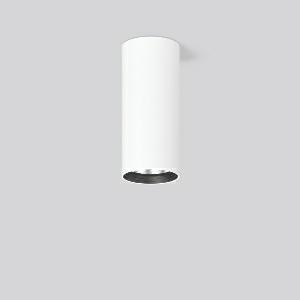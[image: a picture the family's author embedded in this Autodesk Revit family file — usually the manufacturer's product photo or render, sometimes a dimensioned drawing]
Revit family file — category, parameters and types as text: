
# Revit family: heledon_mini_a_931210_002_ff66
name_source: partatom
category: Lighting Fixtures
units: mm (PartAtom-declared; Revit-internal decimal feet)

## family parameters
Cut with Voids When Loaded = No
Host = Face
Light Source = No
Part Type = Normal
Room Calculation Point = No
Round Connector Dimension = Use Diameter
Shared = No

## types (1)
- HELEDON mini A (1 x LED Modul 930, 3650 lm, 3000)
    Apparent Load = 29 VA
    Approval mark = CE
    CIE Flux Codes = 95 99 100 100 100
    Color Rendering = 90
    Color Temperature = 3000
    Default Elevation = 1800 mm
    Description = Series: HELEDON mini
Cylindrical surface-mounted downlight. Housing: die-cast aluminium, powder-coated. Internal ceiling frame polycarbonate with bayonet mounting. Black plastic ring and recessed LED to prevent glare from the side. Optical assembly with reflector made of MIRO-Silver with 98% total light reflection for outstanding efficiency - can be changed without tools. Best colour rendering index Ra>90. Suitable for Ceiling mounting. Easy installation with a separate ceiling frame with bayonet mounting and plug connection. Driver integrated. Connected via plug-in connector. High quality converter without flickering and stroboscopic effect. The following accessories can be mounted without use of tools: interchangeable lenses, decorative glasses, honeycomb louvre, clear and frosted diffusers, white interchangeable plastic ring. 
Colour: traffic white, matt (RAL 9016)
Diameter: 87 mm
Height: 197 mm
Lamp: LED
Socket: without socket
Colour temperature: 3000K
Colour rendering index (CRI): 92
System power: 29 W
Rated luminous flux: 3650 lm
Luminous efficiency: 126 lm/W
Control gear: Regulated power supply
Protection class: I
Type of protection: IP 20
    Height = 197 mm
    Lamp = 1 x LED Modul 930
    Lamp Light Flux = 3650 lm
    Lamp count = 1
    Length = 87 mm
    Lifetime = 50000 h
    Luminous efficacy = 126 lm/W
    Manufacturer = RZB
    ModVariant = No
    Model = 931210.002
    Mounting Place = Ceiling
    Mounting Type = Surface mounted
    Number of Poles = 1
    OnlyDefault = Yes
    Power Factor = 1
    Product Name = HELEDON mini A
    Product group = Surface mounted downlights
    ProductGroupID = 302
    Protection Class = Protection class I
    Protection Degree = IP 20
    RLX_Detail_Level = 1
    RLX_Emergency_Light_Flux = 0 lm
    RLX_Emergency_Type = 0
    RLX_Emergency_Type_DB = No
    RlxData = <blob elided: 106461 chars, md5=3032ebcd>
    Socket = socket
    Standby Power = 0 W
    System Light Flux = 3650 lm
    System Power = 29 W
    Type Comments = Product without accessories
    Type Image = 931188.002.jpg
    URL = http://relux.com
    VarID = ---
    Voltage = 230 V
    Voltage Range = 220-240 V
    Weight = 0.00 kg
    Width = 0 mm  [stored 0 ft]

note: [stored X ft] marks values corroborated as IEEE doubles in the binary element streams (Revit-internal decimal feet)

## geometry (parser evidence)
native form markers: Blend x4, Sweep x9
no freeform markers — native parametric forms only
